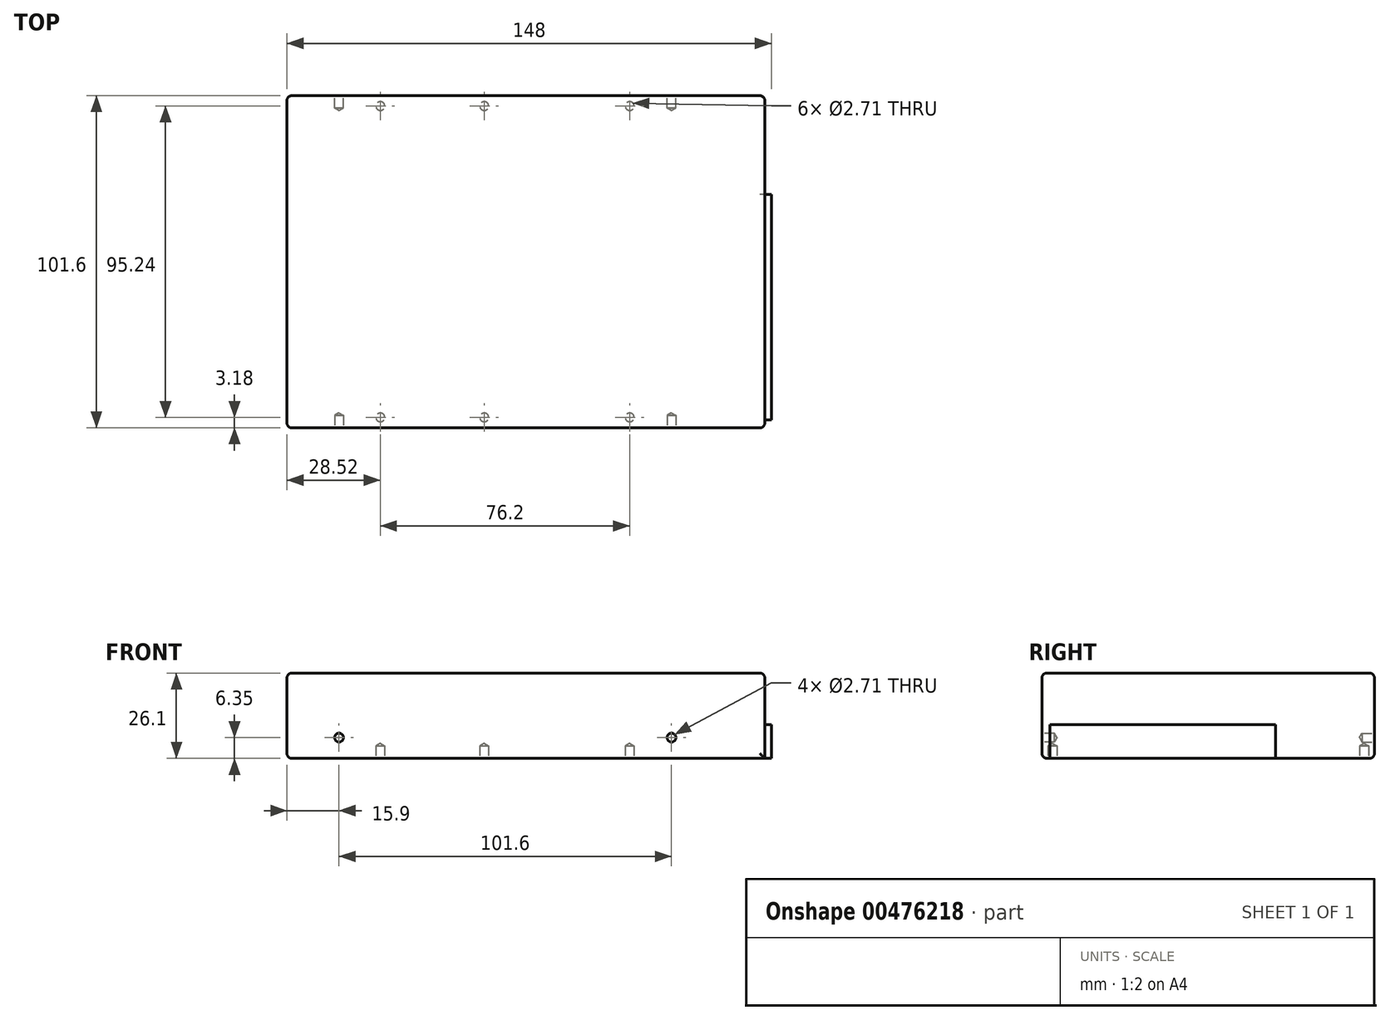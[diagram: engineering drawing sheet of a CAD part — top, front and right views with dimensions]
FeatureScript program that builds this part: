
annotation { "Feature Type Name" : "Feature", "Feature Type Description" : "" }
export const myFeature = defineFeature(function(context is Context, id is Id, definition is map)
    precondition{}
    {
        {
            var Q0;
            Q0=qCreatedBy(makeId("Top.planeOp"),FACE);
            var sketch = newSketch(context, id + "F0", { "sketchPlane" : qUnion([Q0])});
            skLineSegment(sketch, "E0.bottom", {"start": v(-73, 50.8) * mm, "end": v(73, 50.8) * mm});
            skLineSegment(sketch, "E0.top", {"start": v(-73, -50.8) * mm, "end": v(73, -50.8) * mm});
            skLineSegment(sketch, "E0.left", {"start": v(-73, 50.8) * mm, "end": v(-73, -50.8) * mm});
            skLineSegment(sketch, "E0.right", {"start": v(73, 50.8) * mm, "end": v(73, -50.8) * mm});
            skSolve(sketch);
        }
        {
            var Q0;
            Q0=makeQuery(id+"F0.imprint","IMPRINT",FACE,{"disambiguationData":[TD([[makeQuery(id+"F0.imprint","IMPRINT",EDGE,{"derivedFrom":sQuery(id+"F0.wireOp",EDGE,"E0.bottom")}),-1.0]])]});
            extrude(context, id + "F1", {"entities" : qUnion([Q0]), "depth" : 26.1 * mm});
        }
        {
            var Q0;
            Q0=makeQuery(id+"F1.opExtrude","CAP_FACE",FACE,{"disambiguationData":[OSD([sQuery(id+"F0.wireOp",EDGE,"E0.bottom"),sQuery(id+"F0.wireOp",EDGE,"E0.top"),sQuery(id+"F0.wireOp",EDGE,"E0.left"),sQuery(id+"F0.wireOp",EDGE,"E0.right")])],"isStart":true});
            var sketch = newSketch(context, id + "F2", { "sketchPlane" : qUnion([Q0])});
            skLineSegment(sketch, "E1", {"start": v(-73, 47.62) * mm, "end": v(73, 47.62) * mm, "construction": true});
            skPoint(sketch, "E2", {"position": v(31.72, 47.62) * mm});
            skPoint(sketch, "E3", {"position": v(-12.73, 47.62) * mm});
            skPoint(sketch, "E4", {"position": v(-44.48, 47.62) * mm});
            skPoint(sketch, "E5.MirrorP", {"position": v(-44.48, -47.62) * mm});
            skPoint(sketch, "E6.MirrorP", {"position": v(-12.73, -47.62) * mm});
            skPoint(sketch, "E7.MirrorP", {"position": v(31.72, -47.62) * mm});
            skSolve(sketch);
        }
        {
            var Q0;
            Q0=makeQuery(id+"F1.opExtrude","SWEPT_FACE",FACE,{"disambiguationData":[OSD([sQuery(id+"F0.wireOp",EDGE,"E0.top")])]});
            var sketch = newSketch(context, id + "F3", { "sketchPlane" : qUnion([Q0])});
            skLineSegment(sketch, "E8", {"start": v(73, 6.35) * mm, "end": v(-73, 6.35) * mm, "construction": true});
            skPoint(sketch, "E9", {"position": v(44.5, 6.35) * mm});
            skPoint(sketch, "E10", {"position": v(-57.1, 6.35) * mm});
            skSolve(sketch);
        }
        {
            var Q0;
            Q0=makeQuery(id+"F1.opExtrude","SWEPT_FACE",FACE,{"disambiguationData":[OSD([sQuery(id+"F0.wireOp",EDGE,"E0.bottom")])]});
            var sketch = newSketch(context, id + "F4", { "sketchPlane" : qUnion([Q0])});
            skPoint(sketch, "E11.0", {"position": v(-44.5, 6.35) * mm});
            skPoint(sketch, "E12.0", {"position": v(57.1, 6.35) * mm});
            skSolve(sketch);
        }
        {
            var Q0;
            Q0=sQuery(id+"F4.wireOp",VERTEX,"E11.0");
            var Q1;
            Q1=sQuery(id+"F4.wireOp",VERTEX,"E12.0");
            var Q2;
            Q2=sQuery(id+"F2.wireOp",VERTEX,"E5.MirrorP");
            var Q3;
            Q3=sQuery(id+"F2.wireOp",VERTEX,"E6.MirrorP");
            var Q4;
            Q4=sQuery(id+"F2.wireOp",VERTEX,"E7.MirrorP");
            var Q5;
            Q5=sQuery(id+"F2.wireOp",VERTEX,"E2");
            var Q6;
            Q6=sQuery(id+"F2.wireOp",VERTEX,"E3");
            var Q7;
            Q7=sQuery(id+"F2.wireOp",VERTEX,"E4");
            var Q8;
            Q8=sQuery(id+"F3.wireOp",VERTEX,"E10");
            var Q9;
            Q9=sQuery(id+"F3.wireOp",VERTEX,"E9");
            var Q10;
            Q10=makeQuery(id+"F1.opExtrude","SWEPT_BODY",BODY,{"disambiguationData":[OSD([sQuery(id+"F0.wireOp",EDGE,"E0.bottom"),sQuery(id+"F0.wireOp",EDGE,"E0.top"),sQuery(id+"F0.wireOp",EDGE,"E0.left"),sQuery(id+"F0.wireOp",EDGE,"E0.right")])]});
            hole(context, id + "F5", {"style" : HoleStyle.SIMPLE, "endStyle" : HoleEndStyle.BLIND, "standardTappedOrClearance" : lookupTablePath({ "standard" : "ANSI", "engagement" : "75%", "pitch" : "32 tpi", "size" : "#6", "type" : "Tapped" }), "standardBlindInLast" : lookupTablePath({ "standard" : "ANSI", "engagement" : "75%", "pitch" : "32 tpi", "size" : "#6", "type" : "Tapped" }), "holeDiameter" : 2.7 * mm, "showTappedDepth" : true, "holeDepth" : 3.8 * mm, "isTappedThrough" : true, "tappedDepth" : 3.8 * mm, "tapClearance" : 0, "locations" : qUnion([Q0, Q1, Q2, Q3, Q4, Q5, Q6, Q7, Q8, Q9]), "scope" : qUnion([Q10]), "majorDiameter" : 3.5 * mm});
        }
        {
            var Q0;
            Q0=makeQuery(id+"F1.opExtrude","SWEPT_FACE",FACE,{"disambiguationData":[OSD([sQuery(id+"F0.wireOp",EDGE,"E0.right")])]});
            var sketch = newSketch(context, id + "F6", { "sketchPlane" : qUnion([Q0])});
            skLineSegment(sketch, "E13.bottom", {"start": v(-48.42, 10.33) * mm, "end": v(20.6, 10.33) * mm});
            skLineSegment(sketch, "E13.top", {"start": v(-48.42, 0) * mm, "end": v(20.6, 0) * mm});
            skLineSegment(sketch, "E13.left", {"start": v(-48.42, 10.33) * mm, "end": v(-48.42, 0) * mm});
            skLineSegment(sketch, "E13.right", {"start": v(20.6, 10.33) * mm, "end": v(20.6, 0) * mm});
            skSolve(sketch);
        }
        {
            var Q0;
            Q0=makeQuery(id+"F6.imprint","IMPRINT",FACE,{"disambiguationData":[TD([[makeQuery(id+"F6.imprint","IMPRINT",EDGE,{"derivedFrom":sQuery(id+"F6.wireOp",EDGE,"E13.bottom")}),-1.0]])]});
            extrude(context, id + "F7", {"entities" : qUnion([Q0]), "operationType" : NewBodyOperationType.ADD, "depth" : 2 * mm});
        }
        {
            var Q0;
            Q0=makeQuery(id+"F1.opExtrude","CAP_EDGE",EDGE,{"disambiguationData":[OSD([sQuery(id+"F0.wireOp",EDGE,"E0.bottom")])],"isStart":true});
            var Q1;
            Q1=makeQuery(id+"F1.opExtrude","CAP_FACE",FACE,{"disambiguationData":[OSD([sQuery(id+"F0.wireOp",EDGE,"E0.bottom"),sQuery(id+"F0.wireOp",EDGE,"E0.top"),sQuery(id+"F0.wireOp",EDGE,"E0.left"),sQuery(id+"F0.wireOp",EDGE,"E0.right")])],"isStart":false});
            var Q2;
            Q2=makeQuery(id+"F1.opExtrude","SWEPT_FACE",FACE,{"disambiguationData":[OSD([sQuery(id+"F0.wireOp",EDGE,"E0.left")])]});
            var Q3;
            Q3=makeQuery(id+"F1.opExtrude","CAP_EDGE",EDGE,{"disambiguationData":[OSD([sQuery(id+"F0.wireOp",EDGE,"E0.top")])],"isStart":true});
            var Q4;
            {var subQ0=sQuery(id+"F0.wireOp",EDGE,"E0.right");var subQ1=sQuery(id+"F0.wireOp",EDGE,"E0.bottom");Q4=makeQuery(id+"F7.boolean.opBoolean","SPLIT",EDGE,{"disambiguationData":[TD([makeQuery(id+"F1.opExtrude","SWEPT_FACE",FACE,{"disambiguationData":[OSD([subQ1])]})])],"derivedFrom":makeQuery(id+"F1.opExtrude","CAP_EDGE",EDGE,{"disambiguationData":[OSD([subQ0])],"isStart":true})});}
            var Q5;
            Q5=makeQuery(id+"F1.opExtrude","SWEPT_EDGE",EDGE,{"disambiguationData":[OSD([sQuery(id+"F0.wireOp",EDGE,"E0.top"),sQuery(id+"F0.wireOp",EDGE,"E0.right")])]});
            var Q6;
            Q6=makeQuery(id+"F1.opExtrude","SWEPT_EDGE",EDGE,{"disambiguationData":[OSD([sQuery(id+"F0.wireOp",EDGE,"E0.bottom"),sQuery(id+"F0.wireOp",EDGE,"E0.right")])]});
            fillet(context, id + "F8", {"entities" : qUnion([Q0, Q1, Q2, Q3, Q4, Q5, Q6]), "radius" : 1.5 * mm, "tangentPropagation" : true, "allowEdgeOverflow" : false});
        }
    });
